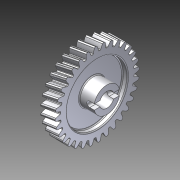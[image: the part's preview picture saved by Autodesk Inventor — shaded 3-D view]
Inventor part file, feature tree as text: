
AUTODESK INVENTOR PART (.ipt)
format: ipt  version: 2014 SP1 (Build 180222100, 222)  size: 4,015,616 bytes
history: native  units: in
note: dims shown in document units (in); Inventor stores cm internally (conversion verified against a paired STEP export)
features: fillet x1, imported_body x1
ambient origin geometry x8: Origin, YZ Plane, XZ Plane, XY Plane, X Axis, Y Axis, Z Axis, Center Point
bodies: Body1 (feature_tree)
feature tree (2):
  fillet  "Fillet2"  [1 undecoded]
  imported_body  "Base1"
note: 1 required parameter value undecoded (feature->parameter linkage not recoverable at this tier; creation-order binding heuristic only, values carry confidence <= 0.55)
